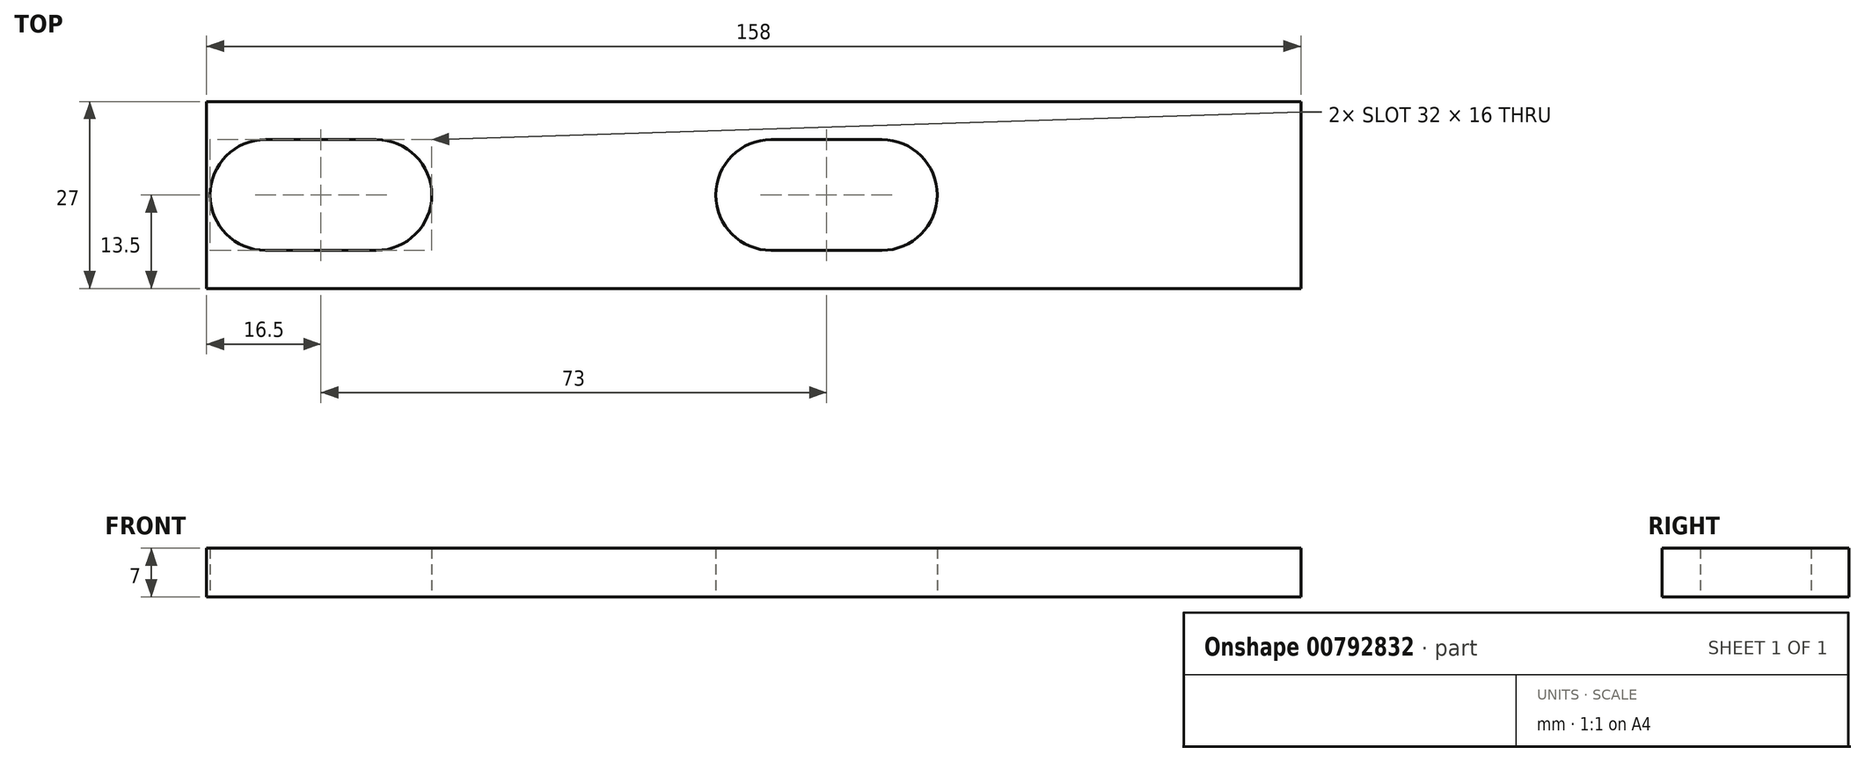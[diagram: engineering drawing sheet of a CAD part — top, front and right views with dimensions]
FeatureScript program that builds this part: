
annotation { "Feature Type Name" : "Feature", "Feature Type Description" : "" }
export const myFeature = defineFeature(function(context is Context, id is Id, definition is map)
    precondition{}
    {
        {
            var Q0;
            Q0=qCreatedBy(makeId("Top.planeOp"),FACE);
            var sketch = newSketch(context, id + "F0", { "sketchPlane" : qUnion([Q0])});
            skLineSegment(sketch, "E0.bottom", {"start": v(260, -13.5) * mm, "end": v(-260, -13.5) * mm});
            skLineSegment(sketch, "E0.top", {"start": v(260, 13.5) * mm, "end": v(-260, 13.5) * mm});
            skLineSegment(sketch, "E0.left", {"start": v(260, -13.5) * mm, "end": v(260, 13.5) * mm});
            skLineSegment(sketch, "E0.right", {"start": v(-260, -13.5) * mm, "end": v(-260, 13.5) * mm});
            skPoint(sketch, "E0.middle", {"position": v(0, 0) * mm});
            skLineSegment(sketch, "E1", {"start": v(-307.4, 0) * mm, "end": v(357.28, 0) * mm, "construction": true});
            skCircle(sketch, "E2", {"center": v(199.5, 0) * mm, "radius": 8 * mm});
            skCircle(sketch, "E3", {"center": v(183.5, 0) * mm, "radius": 8 * mm});
            skCircle(sketch, "E4", {"center": v(126.5, 0) * mm, "radius": 8 * mm});
            skCircle(sketch, "E5", {"center": v(110.5, 0) * mm, "radius": 8 * mm});
            skCircle(sketch, "E6", {"center": v(53.5, 0) * mm, "radius": 8 * mm});
            skCircle(sketch, "E7", {"center": v(37.5, 0) * mm, "radius": 8 * mm});
            skCircle(sketch, "E8", {"center": v(-19.5, 0) * mm, "radius": 8 * mm});
            skCircle(sketch, "E9", {"center": v(-35.5, 0) * mm, "radius": 8 * mm});
            skCircle(sketch, "E10", {"center": v(-92.5, 0) * mm, "radius": 8 * mm});
            skCircle(sketch, "E11", {"center": v(-108.5, 0) * mm, "radius": 8 * mm});
            skLineSegment(sketch, "E12", {"start": v(-108.5, 8) * mm, "end": v(-92.5, 8) * mm});
            skLineSegment(sketch, "E13", {"start": v(-92.5, -8) * mm, "end": v(-108.5, -8) * mm});
            skLineSegment(sketch, "E14", {"start": v(-35.5, -8) * mm, "end": v(-19.5, -8) * mm});
            skLineSegment(sketch, "E15", {"start": v(-19.5, 8) * mm, "end": v(-35.5, 8) * mm});
            skLineSegment(sketch, "E16", {"start": v(37.5, 8) * mm, "end": v(53.5, 8) * mm});
            skLineSegment(sketch, "E17", {"start": v(37.5, -8) * mm, "end": v(53.5, -8) * mm});
            skLineSegment(sketch, "E18", {"start": v(110.5, -8) * mm, "end": v(126.5, -8) * mm});
            skLineSegment(sketch, "E19", {"start": v(126.5, 8) * mm, "end": v(110.5, 8) * mm});
            skLineSegment(sketch, "E20", {"start": v(183.5, 8) * mm, "end": v(199.5, 8) * mm});
            skLineSegment(sketch, "E21", {"start": v(199.5, -8) * mm, "end": v(183.5, -8) * mm});
            skSolve(sketch);
        }
        {
            var Q0;
            Q0 = qSketchRegion(id + "F0", true);
            extrude(context, id + "F1", {"entities" : qUnion([Q0]), "depth" : 7 * mm, "offsetDistance" : 25 * mm});
        }
        {
            var Q0;
            Q0=makeQuery(id+"F1.opExtrude","CAP_FACE",FACE,{"disambiguationData":[OSD([sQuery(id+"F0.wireOp",EDGE,"E0.bottom"),sQuery(id+"F0.wireOp",EDGE,"E0.top"),sQuery(id+"F0.wireOp",EDGE,"E0.left"),sQuery(id+"F0.wireOp",EDGE,"E0.right"),sQuery(id+"F0.wireOp",EDGE,"E2"),sQuery(id+"F0.wireOp",EDGE,"E3"),sQuery(id+"F0.wireOp",EDGE,"E4"),sQuery(id+"F0.wireOp",EDGE,"E5"),sQuery(id+"F0.wireOp",EDGE,"E6"),sQuery(id+"F0.wireOp",EDGE,"E7"),sQuery(id+"F0.wireOp",EDGE,"E8"),sQuery(id+"F0.wireOp",EDGE,"E9"),sQuery(id+"F0.wireOp",EDGE,"E10"),sQuery(id+"F0.wireOp",EDGE,"E11"),sQuery(id+"F0.wireOp",EDGE,"E12"),sQuery(id+"F0.wireOp",EDGE,"E13"),sQuery(id+"F0.wireOp",EDGE,"E14"),sQuery(id+"F0.wireOp",EDGE,"E15"),sQuery(id+"F0.wireOp",EDGE,"E16"),sQuery(id+"F0.wireOp",EDGE,"E17"),sQuery(id+"F0.wireOp",EDGE,"E18"),sQuery(id+"F0.wireOp",EDGE,"E19"),sQuery(id+"F0.wireOp",EDGE,"E20"),sQuery(id+"F0.wireOp",EDGE,"E21")])],"isStart":false});
            var sketch = newSketch(context, id + "F2", { "sketchPlane" : qUnion([Q0])});
            skLineSegment(sketch, "E22", {"start": v(260, 45.02) * mm, "end": v(260, -51.16) * mm});
            skLineSegment(sketch, "E23", {"start": v(102, -51.16) * mm, "end": v(102, 45.02) * mm});
            skLineSegment(sketch, "E24", {"start": v(-56, 45.02) * mm, "end": v(-56, -51.16) * mm});
            skLineSegment(sketch, "E25", {"start": v(-214, -51.16) * mm, "end": v(-214, 45.02) * mm});
            skLineSegment(sketch, "E26", {"start": v(-264, 45.02) * mm, "end": v(-264, -51.16) * mm});
            skLineSegment(sketch, "E27", {"start": v(-264, -51.16) * mm, "end": v(-214, -51.16) * mm});
            skLineSegment(sketch, "E28", {"start": v(-214, -51.16) * mm, "end": v(-56, -51.16) * mm});
            skLineSegment(sketch, "E29", {"start": v(-56, -51.16) * mm, "end": v(102, -51.16) * mm});
            skLineSegment(sketch, "E30", {"start": v(102, -51.16) * mm, "end": v(260, -51.16) * mm});
            skLineSegment(sketch, "E31", {"start": v(-264, 45.02) * mm, "end": v(-214, 45.02) * mm});
            skLineSegment(sketch, "E32", {"start": v(-214, 45.02) * mm, "end": v(-56, 45.02) * mm});
            skLineSegment(sketch, "E33", {"start": v(-56, 45.02) * mm, "end": v(102, 45.02) * mm});
            skSolve(sketch);
        }
        {
            var Q0;
            Q0 = qSketchRegion(id + "F2", true);
            extrude(context, id + "F3", {"entities" : qUnion([Q0]), "operationType" : NewBodyOperationType.REMOVE, "oppositeDirection" : true, "depth" : 25 * mm, "offsetDistance" : 25 * mm});
        }
    });
